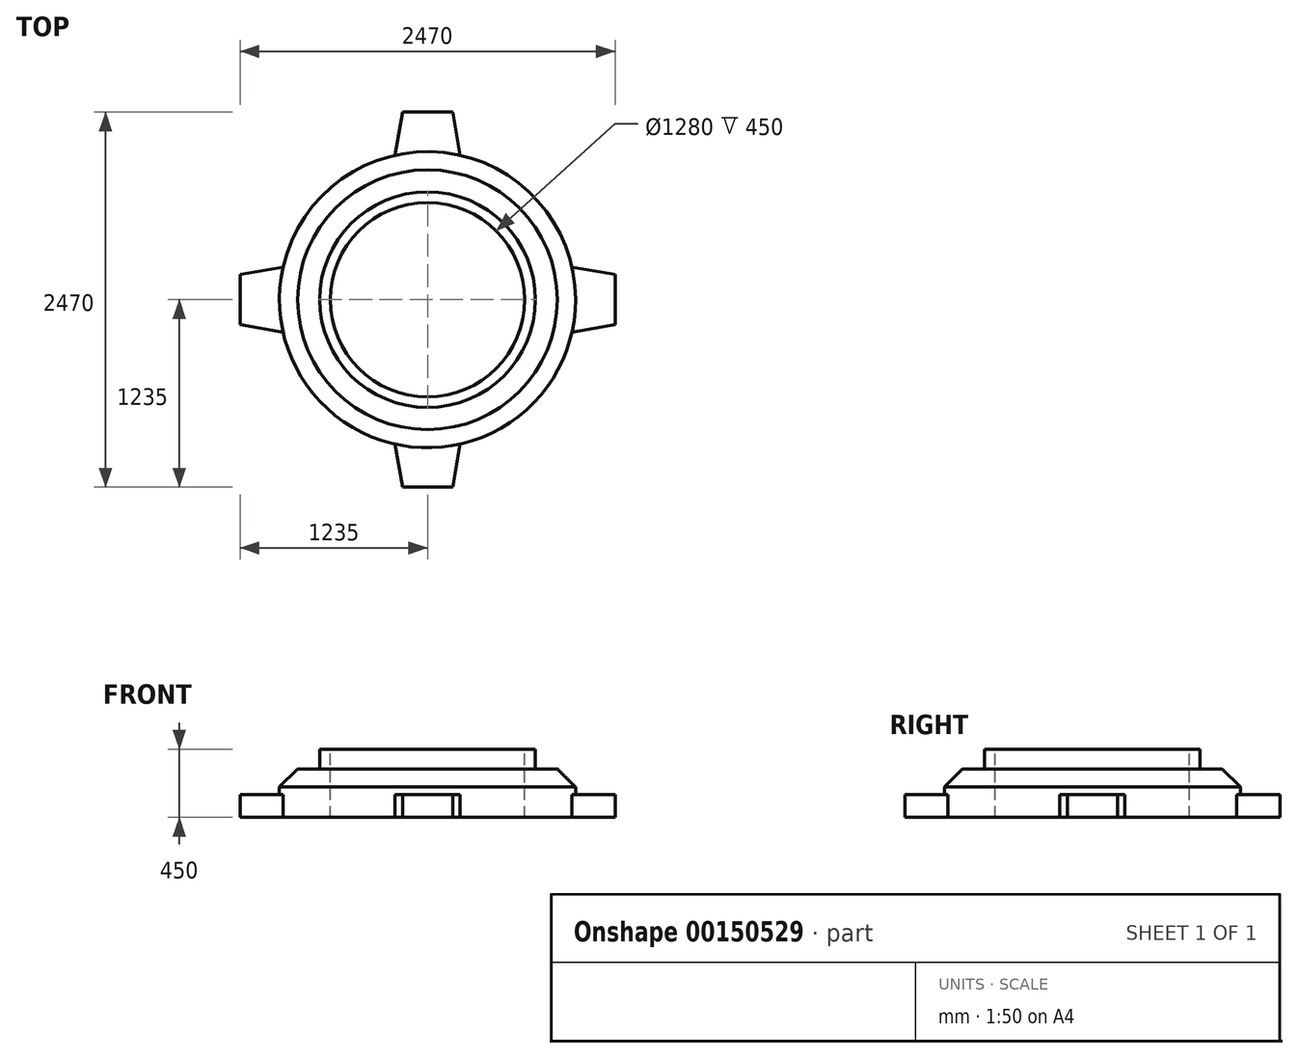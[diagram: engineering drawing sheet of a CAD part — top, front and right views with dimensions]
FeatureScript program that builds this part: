
annotation { "Feature Type Name" : "Feature", "Feature Type Description" : "" }
export const myFeature = defineFeature(function(context is Context, id is Id, definition is map)
    precondition{}
    {
        {
            var Q0;
            Q0=qCreatedBy(makeId("Top.planeOp"),FACE);
            var sketch = newSketch(context, id + "F0", { "sketchPlane" : qUnion([Q0])});
            skCircle(sketch, "E0", {"center": v(0, 0) * mm, "radius": 975 * mm});
            skSolve(sketch);
        }
        {
            var Q0;
            Q0 = qSketchRegion(id + "F0", true);
            extrude(context, id + "F1", {"entities" : qUnion([Q0]), "depth" : 320 * mm});
        }
        {
            var Q0;
            Q0=makeQuery(id+"F1.opExtrude","CAP_FACE",FACE,{"disambiguationData":[OSD([sQuery(id+"F0.wireOp",EDGE,"E0")])],"isStart":false});
            var sketch = newSketch(context, id + "F2", { "sketchPlane" : qUnion([Q0])});
            skCircle(sketch, "E1", {"center": v(0, 0) * mm, "radius": 975 * mm});
            skSolve(sketch);
        }
        {
            var Q0;
            Q0=makeQuery(id+"F1.opExtrude","CAP_FACE",FACE,{"disambiguationData":[OSD([sQuery(id+"F0.wireOp",EDGE,"E0")])],"isStart":false});
            var sketch = newSketch(context, id + "F3", { "sketchPlane" : qUnion([Q0])});
            skCircle(sketch, "E2", {"center": v(0, 0) * mm, "radius": 640 * mm});
            skSolve(sketch);
        }
        {
            var Q0;
            Q0 = qSketchRegion(id + "F3", true);
            extrude(context, id + "F4", {"entities" : qUnion([Q0]), "operationType" : NewBodyOperationType.REMOVE, "endBound" : BoundingType.THROUGH_ALL, "oppositeDirection" : true, "depth" : 25 * mm});
        }
        {
            var Q0;
            Q0=qCreatedBy(makeId("Front.planeOp"),FACE);
            var sketch = newSketch(context, id + "F5", { "sketchPlane" : qUnion([Q0])});
            skLineSegment(sketch, "E3.bottom", {"start": v(215, 150) * mm, "end": v(-215, 150) * mm});
            skPoint(sketch, "E3.middle", {"position": v(0, 0) * mm});
            skLineSegment(sketch, "E4", {"start": v(-215, 0) * mm, "end": v(215, 0) * mm});
            skLineSegment(sketch, "E5", {"start": v(-215, 150) * mm, "end": v(-215, 0) * mm});
            skLineSegment(sketch, "E6", {"start": v(215, 150) * mm, "end": v(215, 0) * mm});
            skSolve(sketch);
        }
        {
            var Q0;
            Q0 = qSketchRegion(id + "F5", true);
            extrude(context, id + "F6", {"entities" : qUnion([Q0]), "operationType" : NewBodyOperationType.ADD, "endBound" : BoundingType.SYMMETRIC, "depth" : 2470 * mm});
        }
        {
            var Q0;
            Q0=qCreatedBy(makeId("Right.planeOp"),FACE);
            var sketch = newSketch(context, id + "F7", { "sketchPlane" : qUnion([Q0])});
            skLineSegment(sketch, "E7.bottom", {"start": v(215, 150) * mm, "end": v(-215, 150) * mm});
            skPoint(sketch, "E7.middle", {"position": v(0, 0) * mm});
            skLineSegment(sketch, "E8", {"start": v(-215, 0) * mm, "end": v(215, 0) * mm});
            skLineSegment(sketch, "E9", {"start": v(-215, 150) * mm, "end": v(-215, 0) * mm});
            skLineSegment(sketch, "E10", {"start": v(215, 150) * mm, "end": v(215, 0) * mm});
            skSolve(sketch);
        }
        {
            var Q0;
            Q0 = qSketchRegion(id + "F7", true);
            extrude(context, id + "F8", {"entities" : qUnion([Q0]), "operationType" : NewBodyOperationType.ADD, "endBound" : BoundingType.SYMMETRIC, "depth" : 2470 * mm});
        }
        {
            var Q0;
            {var subQ0=sQuery(id+"F7.wireOp",EDGE,"E10");var subQ1=sQuery(id+"F7.wireOp",EDGE,"E9");var subQ2=sQuery(id+"F7.wireOp",EDGE,"E7.bottom");Q0=makeQuery(id+"F8.boolean.opBoolean","SPLIT",FACE,{"disambiguationData":[TD([makeQuery(id+"F8.opExtrude","CAP_FACE",FACE,{"disambiguationData":[OSD([subQ2,sQuery(id+"F7.wireOp",EDGE,"E8"),subQ1,subQ0])],"isStart":false})])],"derivedFrom":makeQuery(id+"F8.opExtrude","SWEPT_FACE",FACE,{"disambiguationData":[OSD([subQ2])]})});}
            var sketch = newSketch(context, id + "F9", { "sketchPlane" : qUnion([Q0])});
            skLineSegment(sketch, "E11", {"start": v(951, -215) * mm, "end": v(1235, -165) * mm});
            skLineSegment(sketch, "E12", {"start": v(1235, 165) * mm, "end": v(951, 215) * mm});
            skLineSegment(sketch, "E13", {"start": v(1235, -165) * mm, "end": v(1235, -215) * mm});
            skLineSegment(sketch, "E14", {"start": v(1235, -215) * mm, "end": v(951, -215) * mm});
            skLineSegment(sketch, "E15", {"start": v(1235, 165) * mm, "end": v(1235, 215) * mm});
            skLineSegment(sketch, "E16", {"start": v(1235, 215) * mm, "end": v(951, 215) * mm});
            skSolve(sketch);
        }
        {
            var Q0;
            Q0 = qSketchRegion(id + "F9", true);
            extrude(context, id + "F10", {"entities" : qUnion([Q0]), "operationType" : NewBodyOperationType.REMOVE, "endBound" : BoundingType.THROUGH_ALL, "oppositeDirection" : true, "depth" : 25 * mm});
        }
        {
            var Q0;
            {var subQ0=sQuery(id+"F5.wireOp",EDGE,"E6");var subQ1=sQuery(id+"F5.wireOp",EDGE,"E5");var subQ2=sQuery(id+"F5.wireOp",EDGE,"E3.bottom");Q0=makeQuery(id+"F6.boolean.opBoolean","SPLIT",FACE,{"disambiguationData":[TD([makeQuery(id+"F6.opExtrude","CAP_FACE",FACE,{"disambiguationData":[OSD([subQ2,sQuery(id+"F5.wireOp",EDGE,"E4"),subQ1,subQ0])],"isStart":false})])],"derivedFrom":makeQuery(id+"F6.opExtrude","SWEPT_FACE",FACE,{"disambiguationData":[OSD([subQ2])]})});}
            var sketch = newSketch(context, id + "F11", { "sketchPlane" : qUnion([Q0])});
            skLineSegment(sketch, "E17", {"start": v(-215, -951) * mm, "end": v(-165, -1235) * mm});
            skLineSegment(sketch, "E18", {"start": v(165, -1235) * mm, "end": v(215, -951) * mm});
            skLineSegment(sketch, "E19", {"start": v(-165, -1235) * mm, "end": v(-215, -1235) * mm});
            skLineSegment(sketch, "E20", {"start": v(-215, -1235) * mm, "end": v(-215, -951) * mm});
            skLineSegment(sketch, "E21", {"start": v(165, -1235) * mm, "end": v(215, -1235) * mm});
            skLineSegment(sketch, "E22", {"start": v(215, -1235) * mm, "end": v(215, -951) * mm});
            skSolve(sketch);
        }
        {
            var Q0;
            Q0 = qSketchRegion(id + "F11", true);
            extrude(context, id + "F12", {"entities" : qUnion([Q0]), "operationType" : NewBodyOperationType.REMOVE, "endBound" : BoundingType.THROUGH_ALL, "oppositeDirection" : true, "depth" : 25 * mm});
        }
        {
            var Q0;
            {var subQ0=sQuery(id+"F5.wireOp",EDGE,"E6");var subQ1=sQuery(id+"F5.wireOp",EDGE,"E5");var subQ2=sQuery(id+"F5.wireOp",EDGE,"E3.bottom");Q0=makeQuery(id+"F6.boolean.opBoolean","SPLIT",FACE,{"disambiguationData":[TD([makeQuery(id+"F6.opExtrude","CAP_FACE",FACE,{"disambiguationData":[OSD([subQ2,sQuery(id+"F5.wireOp",EDGE,"E4"),subQ1,subQ0])],"isStart":true})])],"derivedFrom":makeQuery(id+"F6.opExtrude","SWEPT_FACE",FACE,{"disambiguationData":[OSD([subQ2])]})});}
            var sketch = newSketch(context, id + "F13", { "sketchPlane" : qUnion([Q0])});
            skLineSegment(sketch, "E23", {"start": v(-215, 951) * mm, "end": v(-165, 1235) * mm});
            skLineSegment(sketch, "E24", {"start": v(165, 1235) * mm, "end": v(215, 951) * mm});
            skLineSegment(sketch, "E25", {"start": v(-215, 951) * mm, "end": v(-215, 1235) * mm});
            skLineSegment(sketch, "E26", {"start": v(-215, 1235) * mm, "end": v(-165, 1235) * mm});
            skLineSegment(sketch, "E27", {"start": v(165, 1235) * mm, "end": v(215, 1235) * mm});
            skLineSegment(sketch, "E28", {"start": v(215, 1235) * mm, "end": v(215, 951) * mm});
            skSolve(sketch);
        }
        {
            var Q0;
            Q0=makeQuery(id+"F13.imprint","IMPRINT",FACE,{"disambiguationData":[TD([[makeQuery(id+"F13.imprint","IMPRINT",EDGE,{"derivedFrom":sQuery(id+"F13.wireOp",EDGE,"E24")}),1.0]])]});
            var Q1;
            Q1=makeQuery(id+"F13.imprint","IMPRINT",FACE,{"disambiguationData":[TD([[makeQuery(id+"F13.imprint","IMPRINT",EDGE,{"derivedFrom":sQuery(id+"F13.wireOp",EDGE,"E23")}),1.0]])]});
            extrude(context, id + "F14", {"entities" : qUnion([Q0, Q1]), "operationType" : NewBodyOperationType.REMOVE, "endBound" : BoundingType.THROUGH_ALL, "oppositeDirection" : true, "depth" : 25 * mm});
        }
        {
            var Q0;
            {var subQ0=sQuery(id+"F7.wireOp",EDGE,"E9");var subQ1=sQuery(id+"F7.wireOp",EDGE,"E10");var subQ2=sQuery(id+"F7.wireOp",EDGE,"E7.bottom");Q0=makeQuery(id+"F8.boolean.opBoolean","SPLIT",FACE,{"disambiguationData":[TD([makeQuery(id+"F8.opExtrude","CAP_FACE",FACE,{"disambiguationData":[OSD([subQ2,sQuery(id+"F7.wireOp",EDGE,"E8"),subQ0,subQ1])],"isStart":true})])],"derivedFrom":makeQuery(id+"F8.opExtrude","SWEPT_FACE",FACE,{"disambiguationData":[OSD([subQ2])]})});}
            var sketch = newSketch(context, id + "F15", { "sketchPlane" : qUnion([Q0])});
            skLineSegment(sketch, "E29", {"start": v(-951, 215) * mm, "end": v(-1235, 165) * mm});
            skLineSegment(sketch, "E30", {"start": v(-1235, -165) * mm, "end": v(-951, -215) * mm});
            skLineSegment(sketch, "E31", {"start": v(-1235, 165) * mm, "end": v(-1235, 215) * mm});
            skLineSegment(sketch, "E32", {"start": v(-1235, 215) * mm, "end": v(-951, 215) * mm});
            skLineSegment(sketch, "E33", {"start": v(-1235, -165) * mm, "end": v(-1235, -215) * mm});
            skLineSegment(sketch, "E34", {"start": v(-1235, -215) * mm, "end": v(-951, -215) * mm});
            skSolve(sketch);
        }
        {
            var Q0;
            Q0 = qSketchRegion(id + "F15", true);
            extrude(context, id + "F16", {"entities" : qUnion([Q0]), "operationType" : NewBodyOperationType.REMOVE, "endBound" : BoundingType.THROUGH_ALL, "oppositeDirection" : true, "depth" : 25 * mm});
        }
        {
            var Q0;
            Q0=makeQuery(id+"F8.boolean.opBoolean","MERGE",FACE,{"derivedFrom":[makeQuery(id+"F6.boolean.opBoolean","SPLIT",FACE,{"disambiguationData":[TD([makeQuery(id+"F4.boolean.opBoolean","COPY",FACE,{"derivedFrom":makeQuery(id+"F4.opExtrude","SWEPT_FACE",FACE,{"disambiguationData":[OSD([sQuery(id+"F3.wireOp",EDGE,"E2")])]})})])],"derivedFrom":makeQuery(id+"F6.opExtrude","SWEPT_FACE",FACE,{"disambiguationData":[OSD([sQuery(id+"F5.wireOp",EDGE,"E3.bottom")])]})}),makeQuery(id+"F8.opExtrude","SWEPT_FACE",FACE,{"disambiguationData":[OSD([sQuery(id+"F7.wireOp",EDGE,"E7.bottom")])]})]});
            var sketch = newSketch(context, id + "F17", { "sketchPlane" : qUnion([Q0])});
            skCircle(sketch, "E35", {"center": v(0, 0) * mm, "radius": 640 * mm});
            skSolve(sketch);
        }
        {
            var Q0;
            {var subQ4=sQuery(id+"F7.wireOp",EDGE,"E7.bottom");var subQ6=sQuery(id+"F7.wireOp",EDGE,"E10");var subQ17=makeQuery(id+"F8.opExtrude","SWEPT_EDGE",EDGE,{"disambiguationData":[OSD([subQ4,subQ6])]});var subQ19=sQuery(id+"F5.wireOp",EDGE,"E6");var subQ20=makeQuery(id+"F6.opExtrude","SWEPT_FACE",FACE,{"disambiguationData":[OSD([subQ19])]});var subQ25=makeQuery(id+"F8.boolean.opBoolean","SPLIT",EDGE,{"disambiguationData":[TD([subQ20])],"derivedFrom":subQ17});Q0=makeQuery(id+"F17.imprint","IMPRINT",FACE,{"disambiguationData":[TD([[makeQuery(id+"F17.imprint","IMPRINT",EDGE,{"derivedFrom":subQ25}),1.0]])]});}
            var sketch = newSketch(context, id + "F18", { "sketchPlane" : qUnion([Q0])});
            skCircle(sketch, "E36", {"center": v(0, 0) * mm, "radius": 640 * mm});
            skSolve(sketch);
        }
        {
            var Q0;
            Q0 = qSketchRegion(id + "F18", true);
            extrude(context, id + "F19", {"entities" : qUnion([Q0]), "operationType" : NewBodyOperationType.REMOVE, "endBound" : BoundingType.THROUGH_ALL, "oppositeDirection" : true, "depth" : 25 * mm});
        }
        {
            var Q0;
            Q0=makeQuery(id+"F2.imprint","IMPRINT",FACE,{"disambiguationData":[TD([[makeQuery(id+"F2.imprint","IMPRINT",EDGE,{"derivedFrom":sQuery(id+"F2.wireOp",EDGE,"E1")}),1.0]])]});
            var sketch = newSketch(context, id + "F20", { "sketchPlane" : qUnion([Q0])});
            skCircle(sketch, "E37", {"center": v(0, 0) * mm, "radius": 710 * mm});
            skCircle(sketch, "E38", {"center": v(0, 0) * mm, "radius": 640 * mm});
            skSolve(sketch);
        }
        {
            var Q0;
            Q0 = qSketchRegion(id + "F20", true);
            extrude(context, id + "F21", {"entities" : qUnion([Q0]), "operationType" : NewBodyOperationType.ADD, "depth" : 130 * mm});
        }
        {
            var Q0;
            Q0=makeQuery(id+"F1.opExtrude","CAP_EDGE",EDGE,{"disambiguationData":[OSD([sQuery(id+"F0.wireOp",EDGE,"E0")])],"isStart":false});
            chamfer(context, id + "F22", {"entities" : qUnion([Q0]), "width" : 120 * mm, "tangentPropagation" : true});
        }
    });
